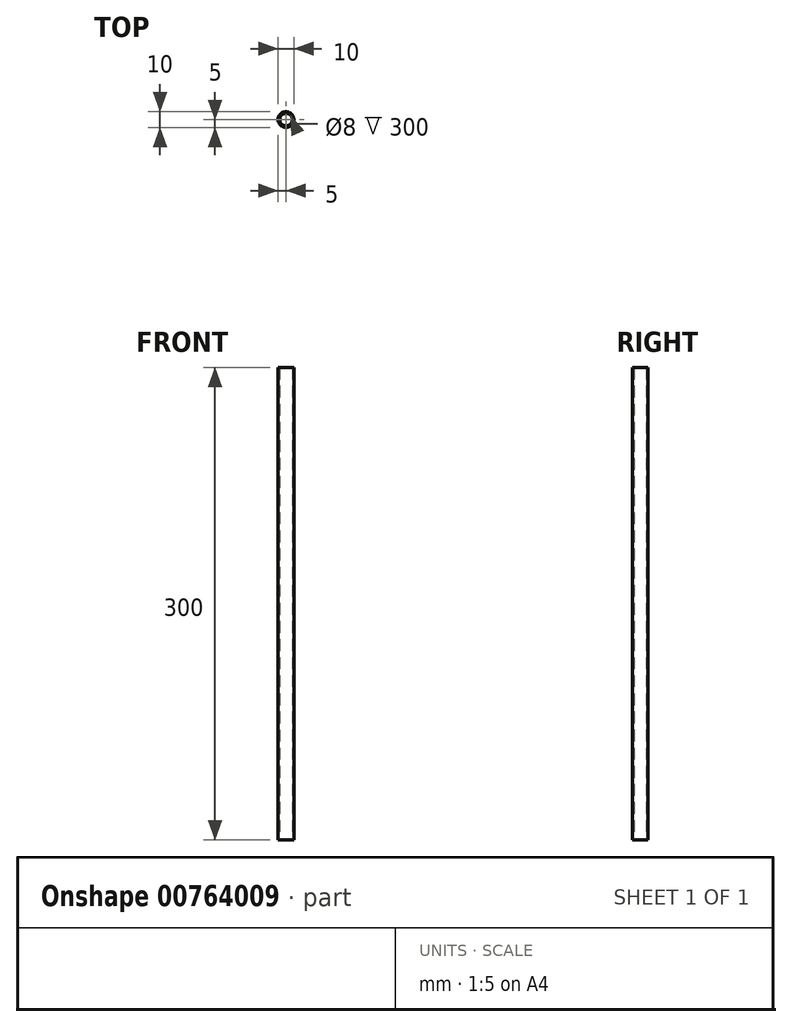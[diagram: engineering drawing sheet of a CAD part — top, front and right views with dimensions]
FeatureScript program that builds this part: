
annotation { "Feature Type Name" : "Feature", "Feature Type Description" : "" }
export const myFeature = defineFeature(function(context is Context, id is Id, definition is map)
    precondition{}
    {
        {
            var Q0;
            Q0=qCreatedBy(makeId("Front.planeOp"),FACE);
            var sketch = newSketch(context, id + "F0", { "sketchPlane" : qUnion([Q0])});
            skLineSegment(sketch, "E0", {"start": v(0, 0) * mm, "end": v(0, 26.9) * mm, "construction": true});
            skLineSegment(sketch, "E1", {"start": v(-4, 0) * mm, "end": v(-4, 300) * mm});
            skLineSegment(sketch, "E2", {"start": v(-4, 300) * mm, "end": v(-5, 300) * mm});
            skLineSegment(sketch, "E3", {"start": v(-5, 300) * mm, "end": v(-5, 0) * mm});
            skLineSegment(sketch, "E4", {"start": v(-5, 0) * mm, "end": v(-4, 0) * mm});
            skSolve(sketch);
        }
        {
            var Q0;
            Q0=makeQuery(id+"F0.imprint","IMPRINT",FACE,{"disambiguationData":[TD([[makeQuery(id+"F0.imprint","IMPRINT",EDGE,{"derivedFrom":sQuery(id+"F0.wireOp",EDGE,"E1")}),1.0]])]});
            var Q1;
            Q1=sQuery(id+"F0.wireOp",EDGE,"E0");
            revolve(context, id + "F1", {"surfaceOperationType" : NewSurfaceOperationType.NEW, "entities" : qUnion([Q0]), "axis" : qUnion([Q1]), "revolveType" : RevolveType.FULL});
        }
    });
